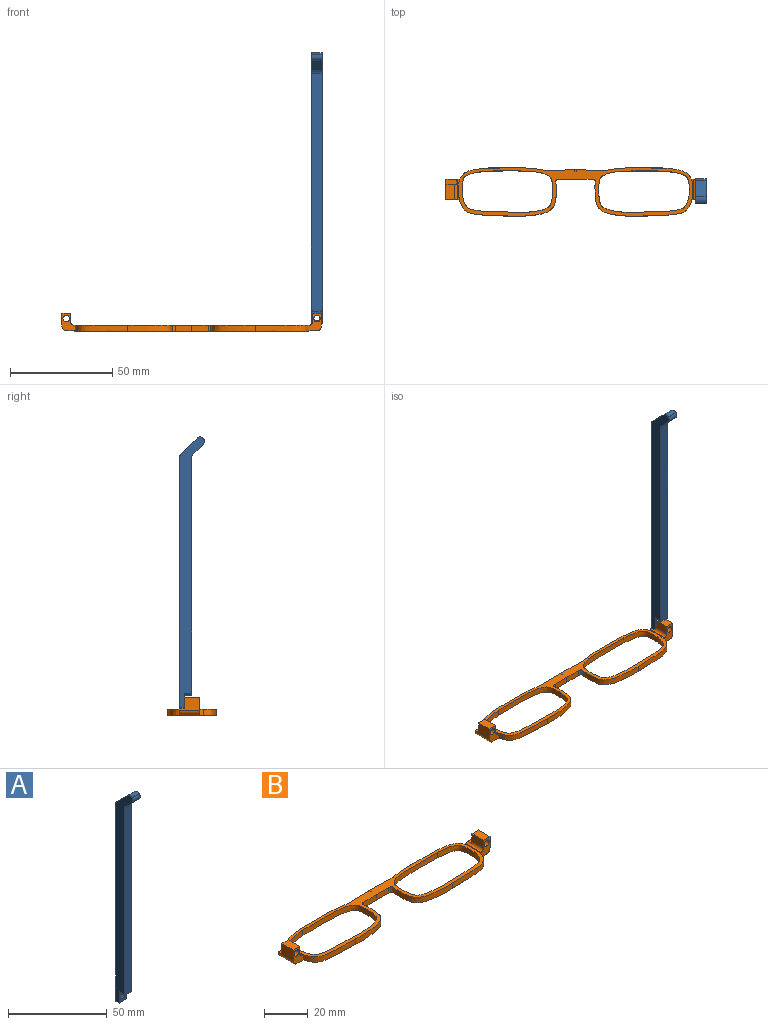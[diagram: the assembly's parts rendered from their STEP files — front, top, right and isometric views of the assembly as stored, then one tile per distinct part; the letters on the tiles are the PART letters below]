
ASSEMBLY  parts=2 mates=1
PART A: 17 faces, bbox 5.3x12.2x132.4 mm
  f0: plane 8.07x8.07mm, normal (0,0.71,0.71), area 60mm2, adj f7,f8,f13,f14
  f1: plane 122.37x5.26mm, normal (0,1,0), area 634mm2, adj f8,f10,f12,f13,f14
  f2: plane 116.17x5.26mm, normal (0,-1,0), area 610.1mm2, adj f5,f11,f13,f14,f15,f16
  f3: plane 5.26x5.07mm, normal (0,-0.71,-0.71), area 37.7mm2, adj f5,f6,f13,f14
  f4: plane 5.26x0.17mm, normal (0,-0.71,0.71), area 1.3mm2, adj f6,f7,f13,f14
  f5: cylinder r=2mm len=5.26mm, axis (1,0,0), area 8.3mm2, adj f2,f3,f13,f14
  f6: cylinder r=2mm len=5.26mm, axis (-1,0,0), area 16.5mm2, adj f3,f4,f13,f14
  f7: cylinder r=2mm len=5.26mm, axis (-1,0,0), area 16.5mm2, adj f0,f4,f13,f14
  f8: cylinder r=2mm len=5.26mm, axis (1,0,0), area 8.3mm2, adj f0,f1,f13,f14
  f9: plane 7.2x5.26mm, normal (0,-1,0), area 23.9mm2, adj f10,f11,f12,f13,f14,f15,f16
  f10: plane 5.26x2.43mm, normal (0,0,-1), area 12.8mm2, adj f1,f9,f13,f14
  f11: plane 3.57x3.26mm, normal (0,0,-1), area 11.6mm2, adj f2,f9,f15,f16
  f12: cylinder r=1.7mm len=3.4mm, axis (0,1,0), area 26mm2, adj f1,f9
  f13: plane 132.44x12.24mm, normal (1,0,0), area 763.2mm2, adj f0,f1,f2,f3,f4,f5,f6,f7
  f14: plane 132.44x12.24mm, normal (-1,0,0), area 763.2mm2, adj f0,f1,f2,f3,f4,f5,f6,f7
  f15: cylinder r=1mm len=3.57mm, axis (0,1,0), area 5.6mm2, adj f2,f9,f11,f14
  f16: cylinder r=1mm len=3.57mm, axis (0,1,0), area 5.6mm2, adj f2,f9,f11,f13
PART B: 55 faces, bbox 126.8x23.8x8.7 mm
  f0: plane 114.48x23.82mm, normal (0,0,-1), area 519.1mm2, adj f6,f7,f8,f9,f10,f11,f12,f13
  f1: plane 114.48x23.82mm, normal (0,0,1), area 519.1mm2, adj f6,f7,f8,f9,f10,f11,f12,f13
  f2: cylinder r=1.6mm len=9.83mm, axis (0,1,0), area 22.1mm2, adj f3,f5,f28,f40,f41,f46
  f3: plane 6.82x3.43mm, normal (0,1,0), area 21.1mm2, adj f2,f18,f28,f29,f30,f31,f46
  f4: plane 6.82x2.95mm, normal (0,1,0), area 18.6mm2, adj f6,f32,f33,f35,f36,f37,f44,f45
  f5: plane 8.63x6.61mm, normal (0,-1,0), area 34.7mm2, adj f2,f7,f28,f29,f30,f31,f41,f43
  f6: extruded ~41.78x6.9mm, area 130.8mm2, adj f0,f1,f4,f10,f16,f32,f33
  f7: extruded ~10.58x3mm, area 7.3mm2, adj f0,f1,f5,f18,f19,f28,f31
  f8: plane 3x0.99mm, normal (-1,0.02,0), area 3mm2, adj f0,f1,f17,f25
  f9: plane 3x0.99mm, normal (1,0.02,0), area 3mm2, adj f0,f1,f16,f24
  f10: extruded ~10.58x3mm, area 7.3mm2, adj f0,f1,f6,f11,f32,f33,f34
  f11: extruded ~25.03x6.25mm, area 82.2mm2, adj f0,f1,f10,f12
  f12: extruded ~21.77x16.81mm, area 100.8mm2, adj f0,f1,f11,f14
  f13: plane 8.05x3mm, normal (0.02,-1,0), area 24.1mm2, adj f0,f1,f15,f21
  f14: cylinder r=1mm len=3mm, axis (0,0,-1), area 3.7mm2, adj f0,f1,f12,f15
  f15: cylinder r=4mm len=3mm, axis (0,0,1), area 3.6mm2, adj f0,f1,f13,f14
  f16: plane 14.78x3mm, normal (-0.02,1,0), area 44.3mm2, adj f0,f1,f6,f9
  f17: plane 14.78x3mm, normal (0.02,1,0), area 44.3mm2, adj f0,f1,f8,f18
  f18: extruded ~41.78x6.9mm, area 130.8mm2, adj f0,f1,f3,f7,f17,f28,f31
  f19: extruded ~25.03x6.25mm, area 82.2mm2, adj f0,f1,f7,f20
  f20: extruded ~21.77x16.81mm, area 100.8mm2, adj f0,f1,f19,f23
  f21: plane 8.05x3mm, normal (-0.02,-1,0), area 24.1mm2, adj f0,f1,f13,f22
  f22: cylinder r=4mm len=3mm, axis (0,0,1), area 3.6mm2, adj f0,f1,f21,f23
  f23: cylinder r=1mm len=3mm, axis (0,0,-1), area 3.7mm2, adj f0,f1,f20,f22
  f24: plane 3x1mm, normal (-1,0.02,0), area 3mm2, adj f0,f1,f9,f27
  f25: plane 3x1mm, normal (1,0.02,0), area 3mm2, adj f0,f1,f8,f26
  f26: plane 3x0.33mm, normal (-0.02,1,0), area 1mm2, adj f0,f1,f25,f27
  f27: plane 3x0.33mm, normal (0.02,1,0), area 1mm2, adj f0,f1,f24,f26
  f28: plane 9.85x0.98mm, normal (0,0,1), area 4.7mm2, adj f2,f3,f5,f7,f18
  f29: plane 9.83x6.23mm, normal (1,0,0), area 48.6mm2, adj f3,f5,f30,f40,f43,f46
  f30: cylinder r=2.4mm len=9.83mm, axis (0,1,0), area 37.1mm2, adj f3,f5,f29,f31
  f31: plane 9.85x4.43mm, normal (0,0,-1), area 38.7mm2, adj f3,f5,f7,f18,f30
  f32: plane 9.85x4.43mm, normal (0,0,-1), area 38.7mm2, adj f4,f6,f10,f34,f36
  f33: plane 9.85x0.98mm, normal (0,0,1), area 4.7mm2, adj f4,f6,f10,f34,f35
  f34: plane 8.63x6.61mm, normal (0,-1,0), area 34.7mm2, adj f10,f32,f33,f35,f36,f37,f39,f42
  f35: cylinder r=1.6mm len=9.83mm, axis (0,1,0), area 20.1mm2, adj f4,f33,f34,f38,f39,f45
  f36: cylinder r=2.4mm len=9.83mm, axis (0,-1,0), area 37.1mm2, adj f4,f32,f34,f37
  f37: plane 9.83x6.23mm, normal (-1,0,0), area 47.4mm2, adj f4,f34,f36,f38,f42,f44
  f38: plane 5.7x5.26mm, normal (0,1,0), area 16.6mm2, adj f35,f37,f39,f42,f44,f45,f47
  f39: plane 7.4x4.2mm, normal (1,0,0), area 31.1mm2, adj f34,f35,f38,f42
  f40: plane 5.2x4.61mm, normal (0,1,0), area 14.2mm2, adj f2,f29,f41,f43,f46,f48
  f41: plane 7.4x4.2mm, normal (-1,0,0), area 31.1mm2, adj f2,f5,f40,f43
  f42: plane 7.4x4.26mm, normal (0,0,1), area 31.5mm2, adj f34,f37,f38,f39
  f43: plane 7.4x4.26mm, normal (0,0,1), area 31.5mm2, adj f5,f29,f40,f41
  f44: plane 5.26x2.43mm, normal (0,0,1), area 12.8mm2, adj f4,f37,f38,f45
  f45: plane 2.43x0.02mm, normal (-1,0,0), area 0mm2, adj f4,f35,f38,f44
  f46: plane 4.61x2.43mm, normal (0,0,1), area 11.2mm2, adj f2,f3,f29,f40
  f47: cylinder r=1.6mm len=7.4mm, axis (0,1,0), area 74.4mm2, adj f34,f38
  f48: cylinder r=1.6mm len=7.4mm, axis (0,1,0), area 74.4mm2, adj f5,f40
  f49: extruded ~3.08x3mm, area 10.7mm2, adj f0,f1,f50,f51
  f50: extruded ~32.12x17.28mm, area 139.4mm2, adj f0,f1,f49,f51
  f51: extruded ~39.62x20.11mm, area 199mm2, adj f0,f1,f49,f50
  f52: extruded ~3.08x3mm, area 10.7mm2, adj f0,f1,f53,f54
  f53: extruded ~39.62x20.11mm, area 199mm2, adj f0,f1,f52,f54
  f54: extruded ~32.12x17.28mm, area 139.4mm2, adj f0,f1,f52,f53
PLACE A t=(31.08,63.19,-1.28)mm
PLACE B t=(-29.62,58.76,-6.91)mm
MATE fastened B.f46 <-> A.f10  axis (0,0,1) through (31.48,64.97,-3.38)mm
